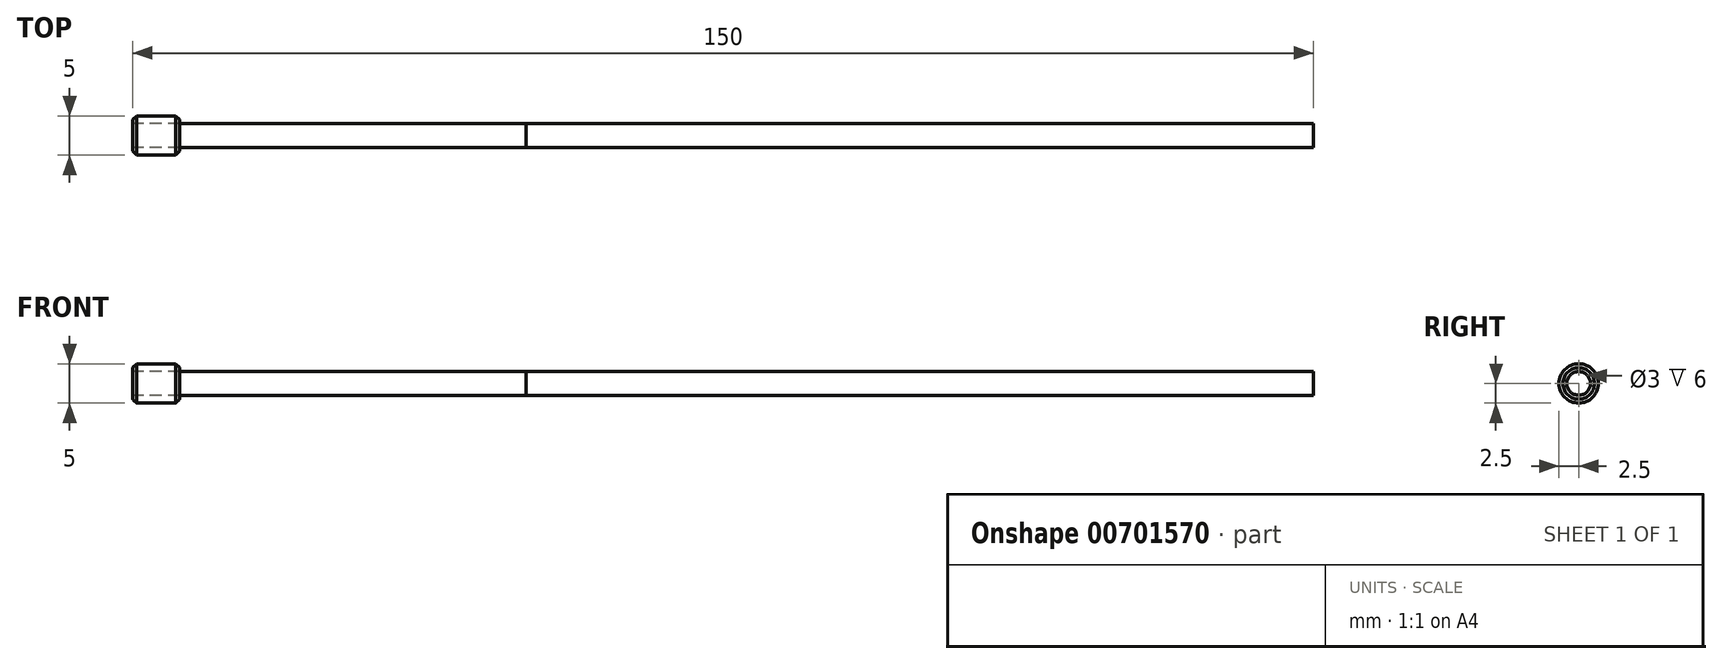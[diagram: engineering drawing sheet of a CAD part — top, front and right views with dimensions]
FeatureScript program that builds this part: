
annotation { "Feature Type Name" : "Feature", "Feature Type Description" : "" }
export const myFeature = defineFeature(function(context is Context, id is Id, definition is map)
    precondition{}
    {
        {
            var Q0;
            Q0=qCreatedBy(makeId("Right.planeOp"),FACE);
            var sketch = newSketch(context, id + "F0", { "sketchPlane" : qUnion([Q0])});
            skCircle(sketch, "E0", {"center": v(0, 0) * mm, "radius": 1.5 * mm});
            skSolve(sketch);
        }
        {
            var Q0;
            Q0 = qSketchRegion(id + "F0", true);
            extrude(context, id + "F1", {"entities" : qUnion([Q0]), "depth" : 150 * mm, "offsetDistance" : 25 * mm});
        }
        {
            var Q0;
            Q0 = qSketchRegion(id + "F0", true);
            extrude(context, id + "F2", {"entities" : qUnion([Q0]), "depth" : 50 * mm, "offsetDistance" : 25 * mm});
        }
        {
            var Q0;
            Q0=qCreatedBy(makeId("Right.planeOp"),FACE);
            var sketch = newSketch(context, id + "F3", { "sketchPlane" : qUnion([Q0])});
            skCircle(sketch, "E1", {"center": v(0, 0) * mm, "radius": 2.5 * mm});
            skCircle(sketch, "E2", {"center": v(0, 0) * mm, "radius": 1.5 * mm});
            skSolve(sketch);
        }
        {
            var Q0;
            Q0 = qSketchRegion(id + "F3", true);
            extrude(context, id + "F4", {"entities" : qUnion([Q0]), "depth" : 6 * mm, "offsetDistance" : 25 * mm});
        }
        {
            var Q0;
            Q0=makeQuery(id+"F4.opExtrude","CAP_EDGE",EDGE,{"disambiguationData":[OSD([sQuery(id+"F3.wireOp",EDGE,"E1")])],"isStart":false});
            var Q1;
            Q1=makeQuery(id+"F4.opExtrude","CAP_EDGE",EDGE,{"disambiguationData":[OSD([sQuery(id+"F3.wireOp",EDGE,"E1")])],"isStart":true});
            chamfer(context, id + "F5", {"entities" : qUnion([Q0, Q1]), "width" : 0.5 * mm, "tangentPropagation" : true});
        }
    });
